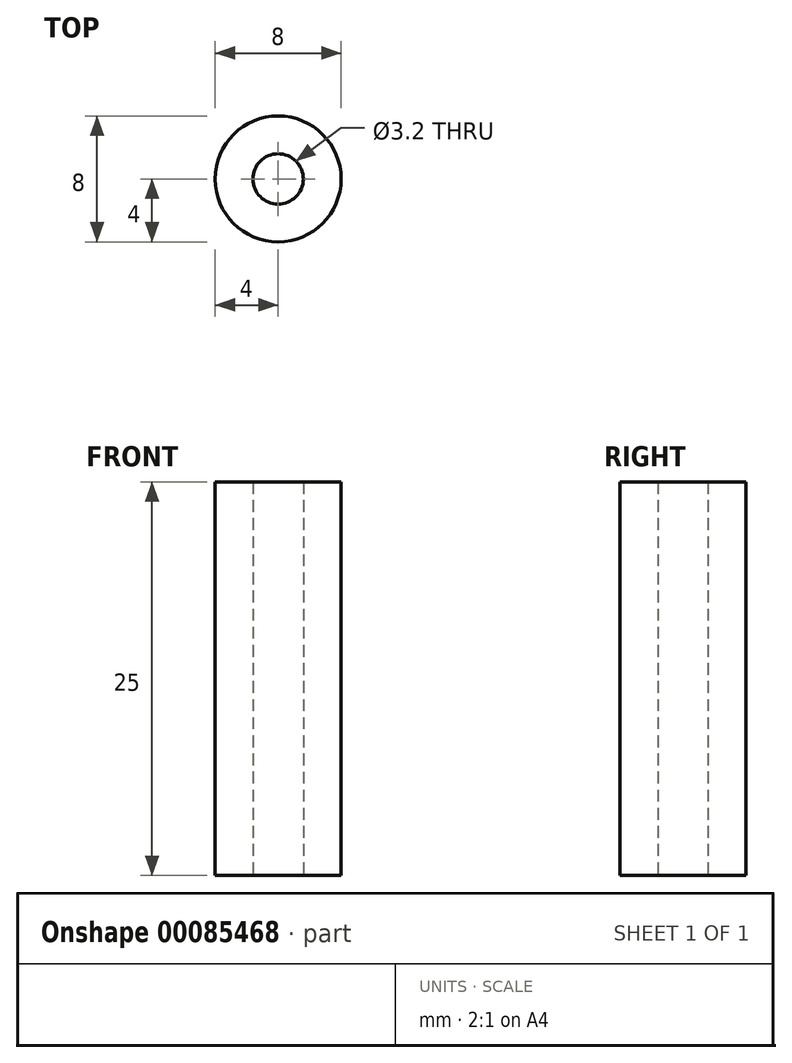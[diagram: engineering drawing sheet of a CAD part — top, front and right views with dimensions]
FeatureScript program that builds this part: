
annotation { "Feature Type Name" : "Feature", "Feature Type Description" : "" }
export const myFeature = defineFeature(function(context is Context, id is Id, definition is map)
    precondition{}
    {
        {
            var Q0;
            Q0=qCreatedBy(makeId("Top.planeOp"),FACE);
            var sketch = newSketch(context, id + "F0", { "sketchPlane" : qUnion([Q0])});
            skPoint(sketch, "E0.middle", {"position": v(0, 0) * mm});
            skLineSegment(sketch, "E1", {"start": v(-2.83, 2.83) * mm, "end": v(2.83, -2.83) * mm, "construction": true});
            skLineSegment(sketch, "E2", {"start": v(2.83, 2.83) * mm, "end": v(-2.83, -2.83) * mm, "construction": true});
            skCircle(sketch, "E3", {"center": v(0, 0) * mm, "radius": 1.6 * mm});
            skCircle(sketch, "E4", {"center": v(0, 0) * mm, "radius": 4 * mm});
            skSolve(sketch);
        }
        {
            var Q0;
            Q0=makeQuery(id+"F0.imprint","IMPRINT",FACE,{"disambiguationData":[TD([[makeQuery(id+"F0.imprint","IMPRINT",EDGE,{"derivedFrom":sQuery(id+"F0.wireOp",EDGE,"E3")}),-1.0]])]});
            extrude(context, id + "F1", {"entities" : qUnion([Q0]), "depth" : 25 * mm});
        }
    });
